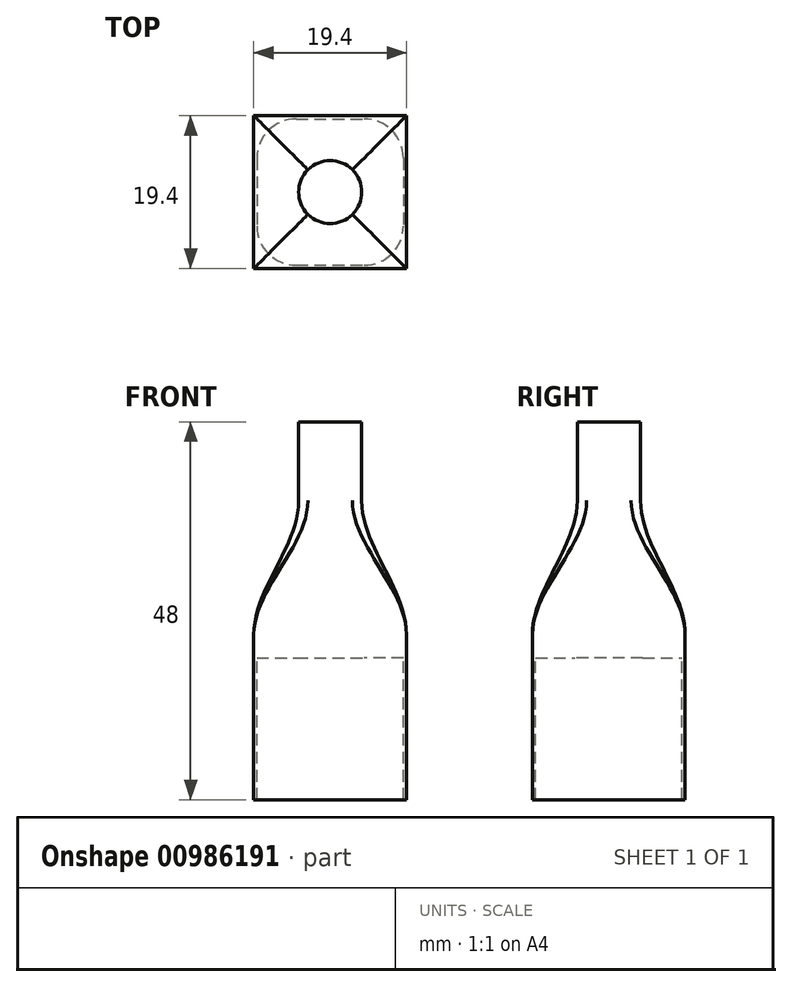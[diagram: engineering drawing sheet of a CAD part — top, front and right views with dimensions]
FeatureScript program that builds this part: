
annotation { "Feature Type Name" : "Feature", "Feature Type Description" : "" }
export const myFeature = defineFeature(function(context is Context, id is Id, definition is map)
    precondition{}
    {
        {
            var Q0;
            Q0=qCreatedBy(makeId("Top.planeOp"),FACE);
            var sketch = newSketch(context, id + "F0", { "sketchPlane" : qUnion([Q0])});
            skLineSegment(sketch, "E0.bottom", {"start": v(-9.7, 9.7) * mm, "end": v(9.7, 9.7) * mm});
            skLineSegment(sketch, "E0.top", {"start": v(-9.7, -9.7) * mm, "end": v(9.7, -9.7) * mm});
            skLineSegment(sketch, "E0.left", {"start": v(-9.7, 9.7) * mm, "end": v(-9.7, -9.7) * mm});
            skLineSegment(sketch, "E0.right", {"start": v(9.7, 9.7) * mm, "end": v(9.7, -9.7) * mm});
            skPoint(sketch, "E0.middle", {"position": v(0, 0) * mm});
            skLineSegment(sketch, "E1.bottom", {"start": v(-9.3, 9.3) * mm, "end": v(9.3, 9.3) * mm});
            skLineSegment(sketch, "E1.top", {"start": v(-9.3, -9.3) * mm, "end": v(9.3, -9.3) * mm});
            skLineSegment(sketch, "E1.left", {"start": v(-9.3, 9.3) * mm, "end": v(-9.3, -9.3) * mm});
            skLineSegment(sketch, "E1.right", {"start": v(9.3, 9.3) * mm, "end": v(9.3, -9.3) * mm});
            skSolve(sketch);
        }
        {
            var Q0;
            Q0=makeQuery(id+"F0.imprint","IMPRINT",FACE,{"disambiguationData":[TD([[makeQuery(id+"F0.imprint","IMPRINT",EDGE,{"derivedFrom":sQuery(id+"F0.wireOp",EDGE,"E0.bottom")}),-1.0]])]});
            var Q1;
            Q1=makeQuery(id+"F0.imprint","IMPRINT",FACE,{"disambiguationData":[TD([[makeQuery(id+"F0.imprint","IMPRINT",EDGE,{"derivedFrom":sQuery(id+"F0.wireOp",EDGE,"E1.bottom")}),-1.0]])]});
            extrude(context, id + "F1", {"entities" : qUnion([Q0, Q1]), "depth" : 3 * mm, "offsetDistance" : 25 * mm});
        }
        {
            var Q0;
            Q0=qCreatedBy(makeId("Top.planeOp"),FACE);
            cPlane(context, id + "F2", {"entities" : qUnion([Q0]), "cplaneType" : CPlaneType.OFFSET, "offset" : 20 * mm, "width" : 150 * mm, "height" : 150 * mm});
        }
        {
            var Q0;
            Q0=qCreatedBy(id+"F2.planeOp",FACE);
            var sketch = newSketch(context, id + "F3", { "sketchPlane" : qUnion([Q0])});
            skCircle(sketch, "E2", {"center": v(0, 0) * mm, "radius": 4 * mm});
            skSolve(sketch);
        }
        {
            var Q0;
            Q0=makeQuery(id+"F3.imprint","IMPRINT",FACE,{"disambiguationData":[TD([[makeQuery(id+"F3.imprint","IMPRINT",EDGE,{"derivedFrom":sQuery(id+"F3.wireOp",EDGE,"E2")}),1.0]])]});
            var Q1;
            Q1=makeQuery(id+"F1.opExtrude","CAP_FACE",FACE,{"disambiguationData":[OSD([sQuery(id+"F0.wireOp",EDGE,"E0.bottom"),sQuery(id+"F0.wireOp",EDGE,"E0.top"),sQuery(id+"F0.wireOp",EDGE,"E0.left"),sQuery(id+"F0.wireOp",EDGE,"E0.right")])],"isStart":false});
            loft(context, id + "F4", {"operationType" : NewBodyOperationType.ADD, "sheetProfilesArray" : [{ "sheetProfileEntities" : qUnion([Q0]) }, { "sheetProfileEntities" : qUnion([Q1]) }], "startCondition" : LoftEndDerivativeType.NORMAL_TO_PROFILE, "startMagnitude" : 1, "endCondition" : LoftEndDerivativeType.NORMAL_TO_PROFILE, "endMagnitude" : 1});
        }
        {
            var Q0;
            Q0=makeQuery(id+"F4.opLoft","CAP_FACE",FACE,{"disambiguationData":[OSD([makeQuery(id+"F3.imprint","IMPRINT",FACE,{"disambiguationData":[TD([[makeQuery(id+"F3.imprint","IMPRINT",EDGE,{"derivedFrom":sQuery(id+"F3.wireOp",EDGE,"E2")}),1.0]])]})])],"isStart":true});
            extrude(context, id + "F5", {"entities" : qUnion([Q0]), "operationType" : NewBodyOperationType.ADD, "depth" : 10 * mm, "offsetDistance" : 25 * mm});
        }
        {
            var Q0;
            Q0=makeQuery(id+"F0.imprint","IMPRINT",FACE,{"disambiguationData":[TD([[makeQuery(id+"F0.imprint","IMPRINT",EDGE,{"derivedFrom":sQuery(id+"F0.wireOp",EDGE,"E0.bottom")}),-1.0]])]});
            extrude(context, id + "F6", {"entities" : qUnion([Q0]), "operationType" : NewBodyOperationType.ADD, "oppositeDirection" : true, "depth" : 18 * mm, "offsetDistance" : 25 * mm});
        }
        {
            var Q0;
            Q0=makeQuery(id+"F6.opExtrude","SWEPT_EDGE",EDGE,{"disambiguationData":[OSD([sQuery(id+"F0.wireOp",EDGE,"E1.bottom"),sQuery(id+"F0.wireOp",EDGE,"E1.left")])]});
            var Q1;
            Q1=makeQuery(id+"F6.opExtrude","SWEPT_EDGE",EDGE,{"disambiguationData":[OSD([sQuery(id+"F0.wireOp",EDGE,"E1.top"),sQuery(id+"F0.wireOp",EDGE,"E1.left")])]});
            var Q2;
            Q2=makeQuery(id+"F6.opExtrude","SWEPT_EDGE",EDGE,{"disambiguationData":[OSD([sQuery(id+"F0.wireOp",EDGE,"E1.top"),sQuery(id+"F0.wireOp",EDGE,"E1.right")])]});
            var Q3;
            Q3=makeQuery(id+"F6.opExtrude","SWEPT_EDGE",EDGE,{"disambiguationData":[OSD([sQuery(id+"F0.wireOp",EDGE,"E1.bottom"),sQuery(id+"F0.wireOp",EDGE,"E1.right")])]});
            fillet(context, id + "F7", {"entities" : qUnion([Q0, Q1, Q2, Q3]), "tangentPropagation" : true, "radius" : 5 * mm, "defaultsChanged" : false, "vertexSettings" : [], "allowEdgeOverflow" : false});
        }
    });
